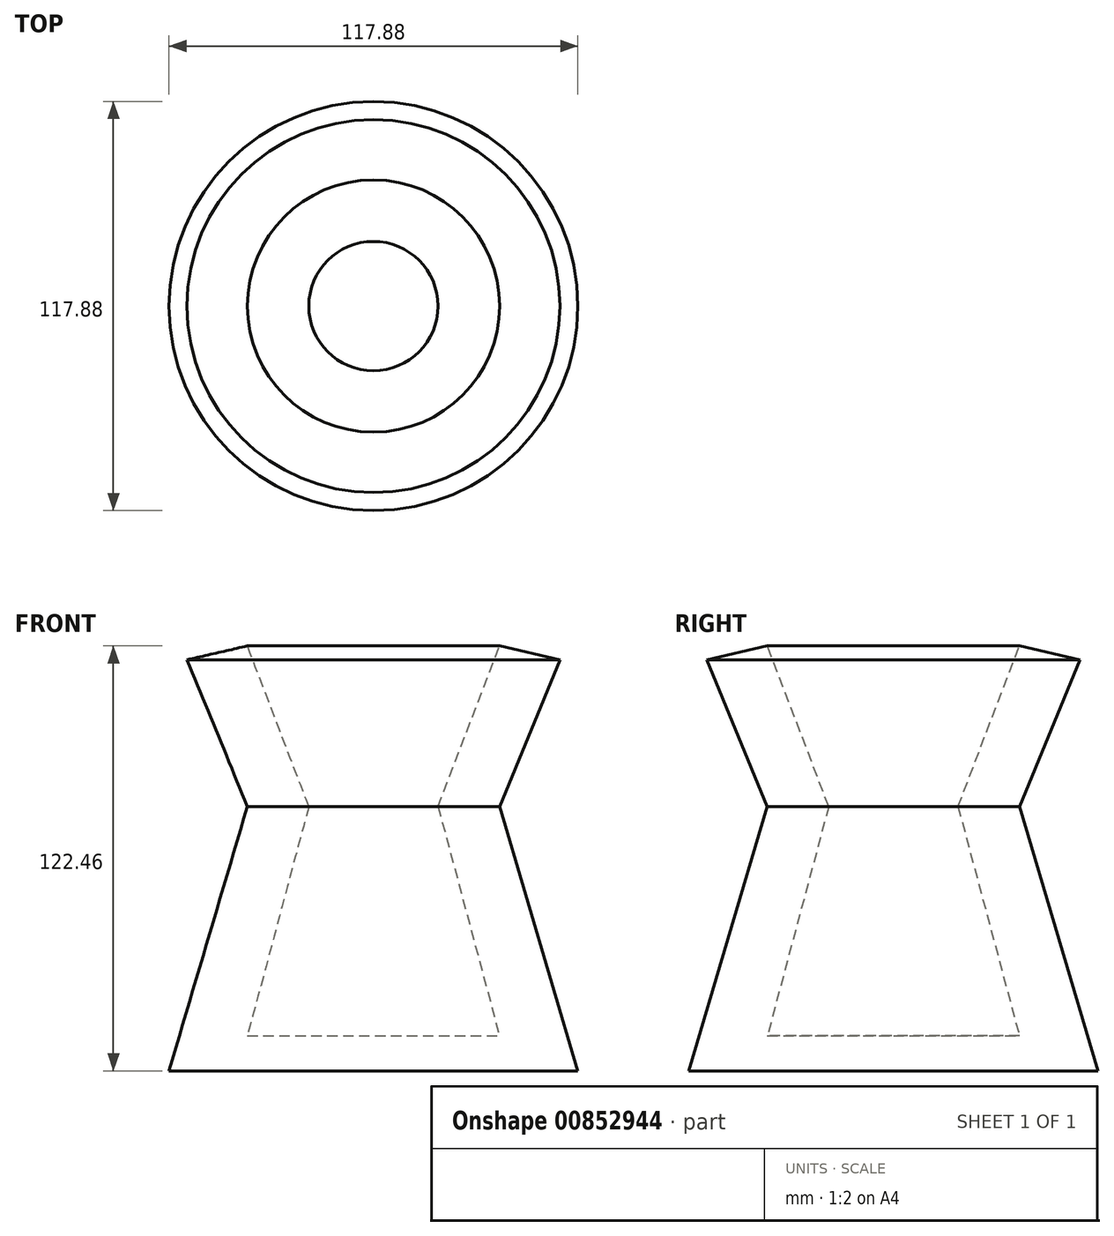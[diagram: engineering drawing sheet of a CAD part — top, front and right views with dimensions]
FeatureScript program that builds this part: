
annotation { "Feature Type Name" : "Feature", "Feature Type Description" : "" }
export const myFeature = defineFeature(function(context is Context, id is Id, definition is map)
    precondition{}
    {
        {
            var Q0;
            Q0=qCreatedBy(makeId("Front.planeOp"),FACE);
            var sketch = newSketch(context, id + "F0", { "sketchPlane" : qUnion([Q0])});
            skLineSegment(sketch, "E0", {"start": v(-53.75, 42.3) * mm, "end": v(-36.34, 0) * mm});
            skLineSegment(sketch, "E1", {"start": v(-36.34, 0) * mm, "end": v(-58.94, -76.2) * mm});
            skLineSegment(sketch, "E2", {"start": v(-58.94, -76.2) * mm, "end": v(0, -76.2) * mm});
            skLineSegment(sketch, "E3", {"start": v(0, -76.2) * mm, "end": v(0, -66.12) * mm});
            skLineSegment(sketch, "E4", {"start": v(0, -66.12) * mm, "end": v(-36.34, -66.12) * mm});
            skLineSegment(sketch, "E5", {"start": v(-36.34, -66.12) * mm, "end": v(-18.63, 0) * mm});
            skLineSegment(sketch, "E6", {"start": v(-18.63, 0) * mm, "end": v(-36.34, 46.27) * mm});
            skLineSegment(sketch, "E7", {"start": v(-36.34, 46.27) * mm, "end": v(-53.75, 42.3) * mm});
            skSolve(sketch);
        }
        {
            var Q0;
            Q0=makeQuery(id+"F0.imprint","IMPRINT",FACE,{"disambiguationData":[TD([[makeQuery(id+"F0.imprint","IMPRINT",EDGE,{"derivedFrom":sQuery(id+"F0.wireOp",EDGE,"E0")}),1.0]])]});
            var Q1;
            Q1=sQuery(id+"F0.wireOp",EDGE,"E3");
            revolve(context, id + "F1", {"surfaceOperationType" : NewSurfaceOperationType.NEW, "entities" : qUnion([Q0]), "axis" : qUnion([Q1]), "revolveType" : RevolveType.FULL});
        }
    });
